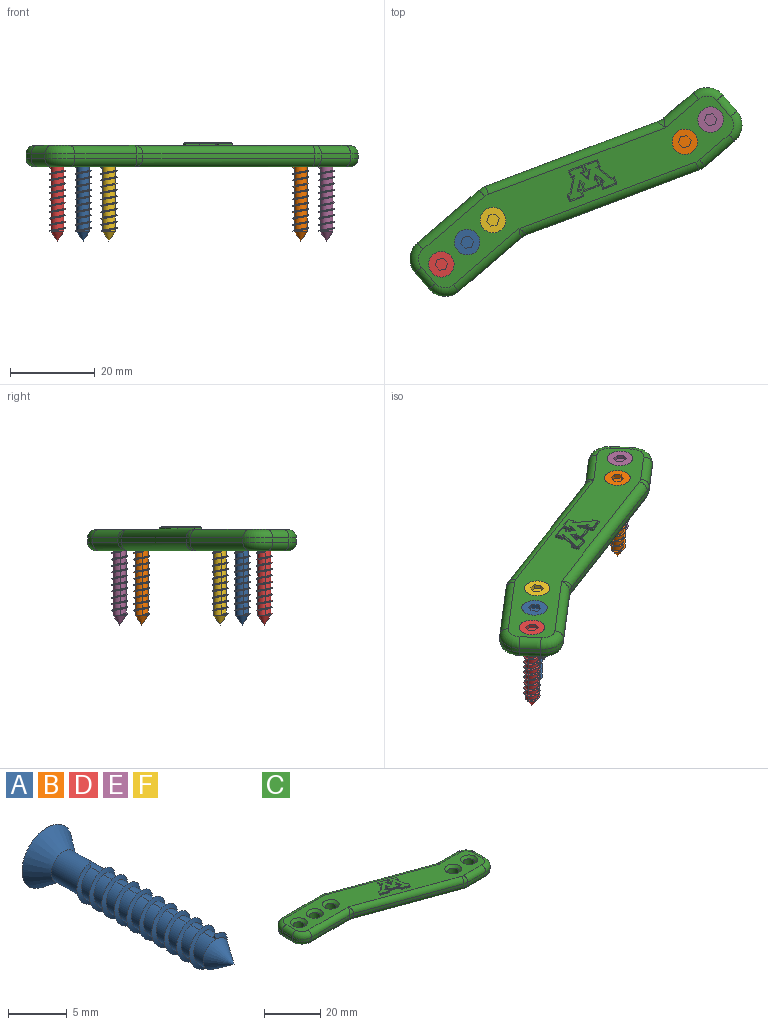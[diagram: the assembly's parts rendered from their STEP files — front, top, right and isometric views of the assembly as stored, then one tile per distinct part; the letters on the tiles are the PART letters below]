
ASSEMBLY  parts=6 mates=5
PART A: 25 faces, bbox 6x22.5x6 mm
  f0: plane 6x6mm, normal (0,1,0), area 22.4mm2, adj f1,f18,f19,f20,f21,f22,f23
  f1: cone r=3mm half-angle=36.9deg, axis (0,1,0), area 35.3mm2, adj f0,f2
  f2: cylinder r=1.5mm len=4.5mm, axis (0,1,0), area 35.3mm2, adj f1,f3,f13,f15
  f3: cylinder r=1.5mm len=3mm, axis (0,1,0), area 11.3mm2, adj f2,f4,f15,f16
  f4: cylinder r=1.5mm len=3mm, axis (0,1,0), area 11.3mm2, adj f3,f5,f15,f16
  f5: cylinder r=1.5mm len=3mm, axis (0,1,0), area 11.3mm2, adj f4,f6,f15,f16
  f6: cylinder r=1.5mm len=3mm, axis (0,1,0), area 11.3mm2, adj f5,f7,f15,f16
  f7: cylinder r=1.5mm len=3mm, axis (0,1,0), area 11.3mm2, adj f6,f8,f15,f16
  f8: cylinder r=1.5mm len=3mm, axis (0,1,0), area 11.3mm2, adj f7,f9,f15,f16
  f9: cylinder r=1.5mm len=3mm, axis (0,1,0), area 11.3mm2, adj f8,f10,f15,f16
  f10: cylinder r=1.5mm len=3mm, axis (0,1,0), area 11.3mm2, adj f9,f11,f15,f16
  f11: cylinder r=1.5mm len=3mm, axis (0,1,0), area 11.3mm2, adj f10,f12,f15,f16
  f12: cylinder r=1.5mm len=3mm, axis (0,1,0), area 7.1mm2, adj f11,f14,f16,f17
  f13: plane 0.4x0.3mm, normal (1,0,0), area 0.1mm2, adj f2,f15,f16
  f14: plane 0.4x0.3mm, normal (-1,0,0), area 0.1mm2, adj f12,f15,f16
  f15: bspline ~15.15x4.39mm, area 46mm2, adj f2,f3,f4,f5,f6,f7,f8,f9
  f16: bspline ~15.15x4.39mm, area 45.9mm2, adj f3,f4,f5,f6,f7,f8,f9,f10
  f17: cone r=1.5mm half-angle=34.3deg, axis (0,1,0), area 12.5mm2, adj f12
  f18: plane 1.5x1mm, normal (1,0,0), area 1.5mm2, adj f0,f19,f23,f24
  f19: plane 1.3x1mm, normal (0.5,0,-0.87), area 1.5mm2, adj f0,f18,f20,f24
  f20: plane 1.3x1mm, normal (-0.5,0,-0.87), area 1.5mm2, adj f0,f19,f21,f24
  f21: plane 1.5x1mm, normal (-1,0,0), area 1.5mm2, adj f0,f20,f22,f24
  f22: plane 1.3x1mm, normal (-0.5,0,0.87), area 1.5mm2, adj f0,f21,f23,f24
  f23: plane 1.3x1mm, normal (0.5,0,0.87), area 1.5mm2, adj f0,f18,f22,f24
  f24: plane 3x2.6mm, normal (0,1,0), area 5.8mm2, adj f18,f19,f20,f21,f22,f23
PART B: same geometry as A
PART C: 65 faces, bbox 83.1x31.2x5.6 mm
  f0: plane 78.29x26.39mm, normal (0,0,1), area 773.2mm2, adj f23,f24,f25,f26,f27,f28,f29,f30
  f1: plane 78.29x26.39mm, normal (0,0,-1), area 779.7mm2, adj f10,f11,f12,f13,f14,f15,f16,f17
  f2: plane 5x1mm, normal (-1,0,0), area 5mm2, adj f18,f26,f44,f47
  f3: plane 19.12x1mm, normal (0,-1,0), area 19.1mm2, adj f16,f24,f47,f50
  f4: plane 40.63x14.79mm, normal (-0.34,-0.94,0), area 43.2mm2, adj f15,f23,f41,f50
  f5: plane 9.12x1mm, normal (0,-1,0), area 9.1mm2, adj f17,f25,f38,f41
  f6: plane 5x1mm, normal (1,0,0), area 5mm2, adj f19,f27,f35,f38
  f7: plane 9.12x1mm, normal (0,1,0), area 9.1mm2, adj f21,f29,f35,f53
  f8: plane 40.63x14.79mm, normal (0.34,0.94,0), area 43.2mm2, adj f22,f30,f32,f53
  f9: plane 19.12x1mm, normal (0,1,0), area 19.1mm2, adj f20,f28,f32,f44
  f10: cylinder r=2mm len=4mm, axis (0,0,1), area 50.3mm2, adj f1,f56
  f11: cylinder r=2mm len=4mm, axis (0,0,1), area 50.3mm2, adj f1,f55
  f12: cylinder r=2mm len=4mm, axis (0,0,1), area 50.3mm2, adj f1,f57
  f13: cylinder r=2mm len=4mm, axis (0,0,1), area 50.3mm2, adj f1,f58
  f14: cylinder r=2mm len=4mm, axis (0,0,1), area 50.3mm2, adj f1,f59
  f15: cylinder r=2mm len=42.47mm, axis (0.94,-0.34,0), area 137.2mm2, adj f1,f4,f42,f49
  f16: cylinder r=2mm len=20.35mm, axis (1,0,0), area 61.5mm2, adj f1,f3,f48,f49
  f17: cylinder r=2mm len=9.12mm, axis (1,0,0), area 28.6mm2, adj f1,f5,f39,f42
  f18: cylinder r=2mm len=5mm, axis (0,-1,0), area 15.7mm2, adj f1,f2,f45,f48
  f19: cylinder r=2mm len=5mm, axis (0,1,0), area 15.7mm2, adj f1,f6,f36,f39
  f20: cylinder r=2mm len=19.12mm, axis (-1,0,0), area 60.1mm2, adj f1,f9,f33,f45
  f21: cylinder r=2mm len=10.35mm, axis (-1,0,0), area 30.1mm2, adj f1,f7,f36,f52
  f22: cylinder r=2mm len=42.47mm, axis (-0.94,0.34,0), area 137.2mm2, adj f1,f8,f33,f52
  f23: cylinder r=2mm len=42.47mm, axis (-0.94,0.34,0), area 137.2mm2, adj f0,f4,f40,f51
  f24: cylinder r=2mm len=20.35mm, axis (-1,0,0), area 61.5mm2, adj f0,f3,f46,f51
  f25: cylinder r=2mm len=9.12mm, axis (-1,0,0), area 28.6mm2, adj f0,f5,f37,f40
  f26: cylinder r=2mm len=5mm, axis (0,1,0), area 15.7mm2, adj f0,f2,f43,f46
  f27: cylinder r=2mm len=5mm, axis (0,-1,0), area 15.7mm2, adj f0,f6,f34,f37
  f28: cylinder r=2mm len=19.12mm, axis (1,0,0), area 60.1mm2, adj f0,f9,f31,f43
  f29: cylinder r=2mm len=10.35mm, axis (1,0,0), area 30.1mm2, adj f0,f7,f34,f54
  f30: cylinder r=2mm len=42.47mm, axis (0.94,-0.34,0), area 137.2mm2, adj f0,f8,f31,f54
  f31: torus R=3mm, axis (0,0,1), area 4.7mm2, adj f0,f28,f30,f32
  f32: cylinder r=5mm len=1.71mm, axis (0,0,-1), area 1.7mm2, adj f8,f9,f31,f33
  f33: torus R=3mm, axis (0,0,1), area 4.7mm2, adj f1,f20,f22,f32
  f34: torus R=3mm, axis (0,0,1), area 21.1mm2, adj f0,f27,f29,f35
  f35: cylinder r=5mm len=5mm, axis (0,0,1), area 7.9mm2, adj f6,f7,f34,f36
  f36: torus R=3mm, axis (0,0,1), area 21.1mm2, adj f1,f19,f21,f35
  f37: torus R=3mm, axis (0,0,1), area 21.1mm2, adj f0,f25,f27,f38
  f38: cylinder r=5mm len=5mm, axis (0,0,-1), area 7.9mm2, adj f5,f6,f37,f39
  f39: torus R=3mm, axis (0,0,1), area 21.1mm2, adj f1,f17,f19,f38
  f40: torus R=3mm, axis (0,0,1), area 4.7mm2, adj f0,f23,f25,f41
  f41: cylinder r=5mm len=1.71mm, axis (0,0,-1), area 1.7mm2, adj f4,f5,f40,f42
  f42: torus R=3mm, axis (0,0,1), area 4.7mm2, adj f1,f15,f17,f41
  f43: torus R=3mm, axis (0,0,1), area 21.1mm2, adj f0,f26,f28,f44
  f44: cylinder r=5mm len=5mm, axis (0,0,1), area 7.9mm2, adj f2,f9,f43,f45
  f45: torus R=3mm, axis (0,0,1), area 21.1mm2, adj f1,f18,f20,f44
  f46: torus R=3mm, axis (0,0,1), area 21.1mm2, adj f0,f24,f26,f47
  f47: cylinder r=5mm len=5mm, axis (0,0,-1), area 7.9mm2, adj f2,f3,f46,f48
  f48: torus R=3mm, axis (0,0,1), area 21.1mm2, adj f1,f16,f18,f47
  f49: bspline ~2.3x2.26mm, area 3.5mm2, adj f15,f16,f50
  f50: cylinder r=5mm len=1.71mm, axis (0,0,1), area 1.7mm2, adj f3,f4,f49,f51
  f51: bspline ~2.3x2.26mm, area 3.5mm2, adj f23,f24,f50
  f52: bspline ~2.3x2.26mm, area 3.5mm2, adj f21,f22,f53
  f53: cylinder r=5mm len=1.71mm, axis (0,0,1), area 1.7mm2, adj f7,f8,f52,f54
  f54: bspline ~2.3x2.26mm, area 3.5mm2, adj f29,f30,f53
  f55: cone r=2mm half-angle=45deg, axis (0,0,1), area 22.2mm2, adj f0,f11
  f56: cone r=2mm half-angle=45deg, axis (0,0,1), area 22.2mm2, adj f0,f10
  f57: cone r=2mm half-angle=45deg, axis (0,0,1), area 22.2mm2, adj f0,f12
  f58: cone r=2mm half-angle=45deg, axis (0,0,1), area 22.2mm2, adj f0,f13
  f59: cone r=2mm half-angle=45deg, axis (0,0,1), area 22.2mm2, adj f0,f14
  f60: extruded ~11.53x8.58mm, area 18.3mm2, adj f0,f61,f62
  f61: extruded ~3.69x2.3mm, area 2.4mm2, adj f0,f60,f62
  f62: plane 11.78x9.87mm, normal (0,0,1), area -11.2mm2, adj f60,f61,f63
  f63: extruded ~10.78x8.71mm, area 10.5mm2, adj f62,f64
  f64: plane 11.12x9.37mm, normal (0,0,1), area 35.6mm2, adj f63
PART D: same geometry as A
PART E: same geometry as A
PART F: same geometry as A
PLACE A rot(axis=(0.65,-0.54,-0.54),114.1deg) t=(4.29,4.51,18.94)mm
PLACE B rot(axis=(0.65,-0.54,-0.54),114.1deg) t=(55.53,28.16,18.94)mm
PLACE C rot(axis=(0,0,1),40.6deg) t=(-11.22,1.1,13.94)mm
PLACE D rot(axis=(0.65,-0.54,-0.54),114.1deg) t=(-1.78,-0.69,18.94)mm
PLACE E rot(axis=(0.65,-0.54,-0.54),114.1deg) t=(61.6,33.36,18.94)mm
PLACE F rot(axis=(0.65,-0.54,-0.54),114.1deg) t=(10.37,9.72,18.94)mm
MATE cylindrical D.f1 <-> C.f14  axis (0,0,-1) through (-1.78,-0.69,16.94)mm
MATE cylindrical A.f1 <-> C.f13  axis (0,0,-1) through (4.29,4.51,16.94)mm
MATE cylindrical F.f1 <-> C.f12  axis (0,0,-1) through (10.37,9.72,16.94)mm
MATE cylindrical E.f1 <-> C.f11  axis (0,0,-1) through (61.6,33.36,16.94)mm
MATE cylindrical B.f1 <-> C.f10  axis (0,0,-1) through (55.53,28.16,16.94)mm
